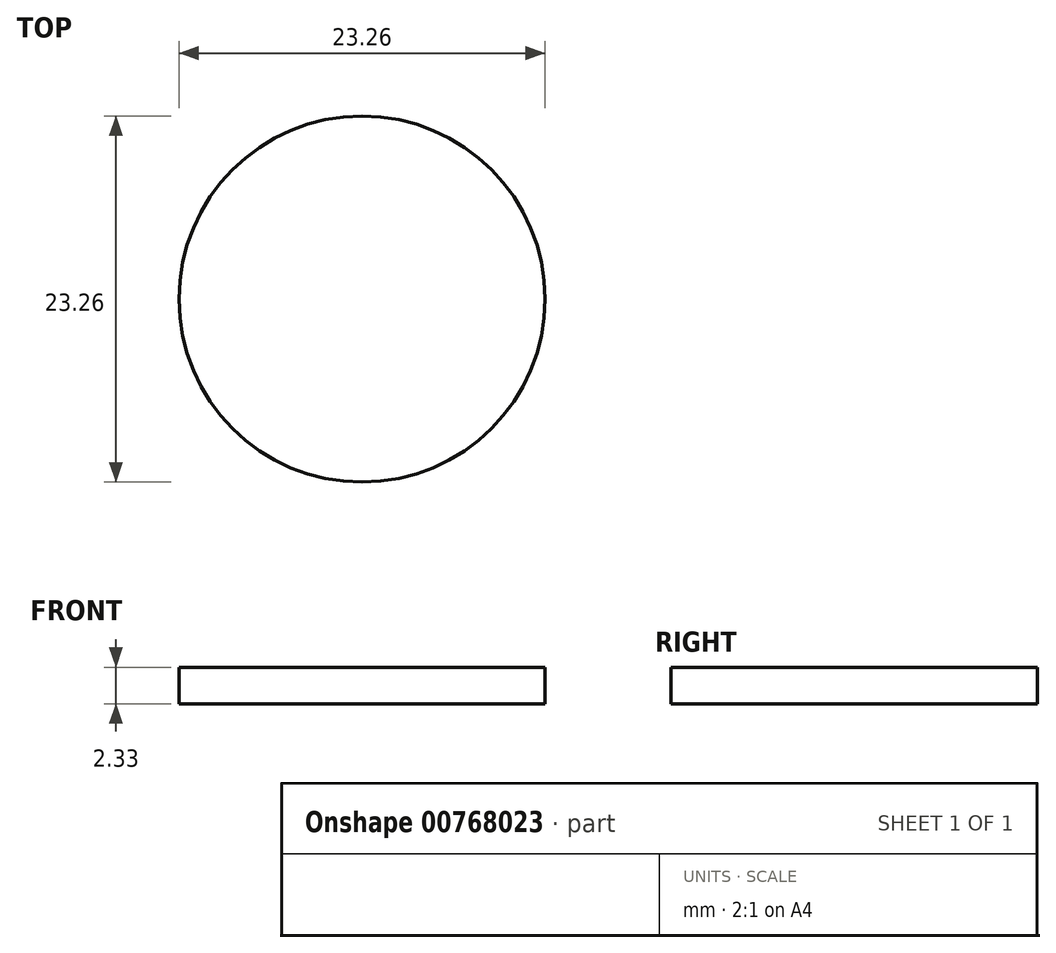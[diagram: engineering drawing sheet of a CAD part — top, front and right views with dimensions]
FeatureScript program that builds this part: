
annotation { "Feature Type Name" : "Feature", "Feature Type Description" : "" }
export const myFeature = defineFeature(function(context is Context, id is Id, definition is map)
    precondition{}
    {
        {
            var Q0;
            Q0=qCreatedBy(makeId("Top.planeOp"),FACE);
            var sketch = newSketch(context, id + "F0", { "sketchPlane" : qUnion([Q0])});
            skCircle(sketch, "E0", {"center": v(0, 0) * mm, "radius": 11.63 * mm});
            skSolve(sketch);
        }
        {
            var Q0;
            Q0 = qSketchRegion(id + "F0", true);
            extrude(context, id + "F1", {"entities" : qUnion([Q0]), "depth" : 2.33 * mm, "offsetDistance" : 25 * mm});
        }
    });
